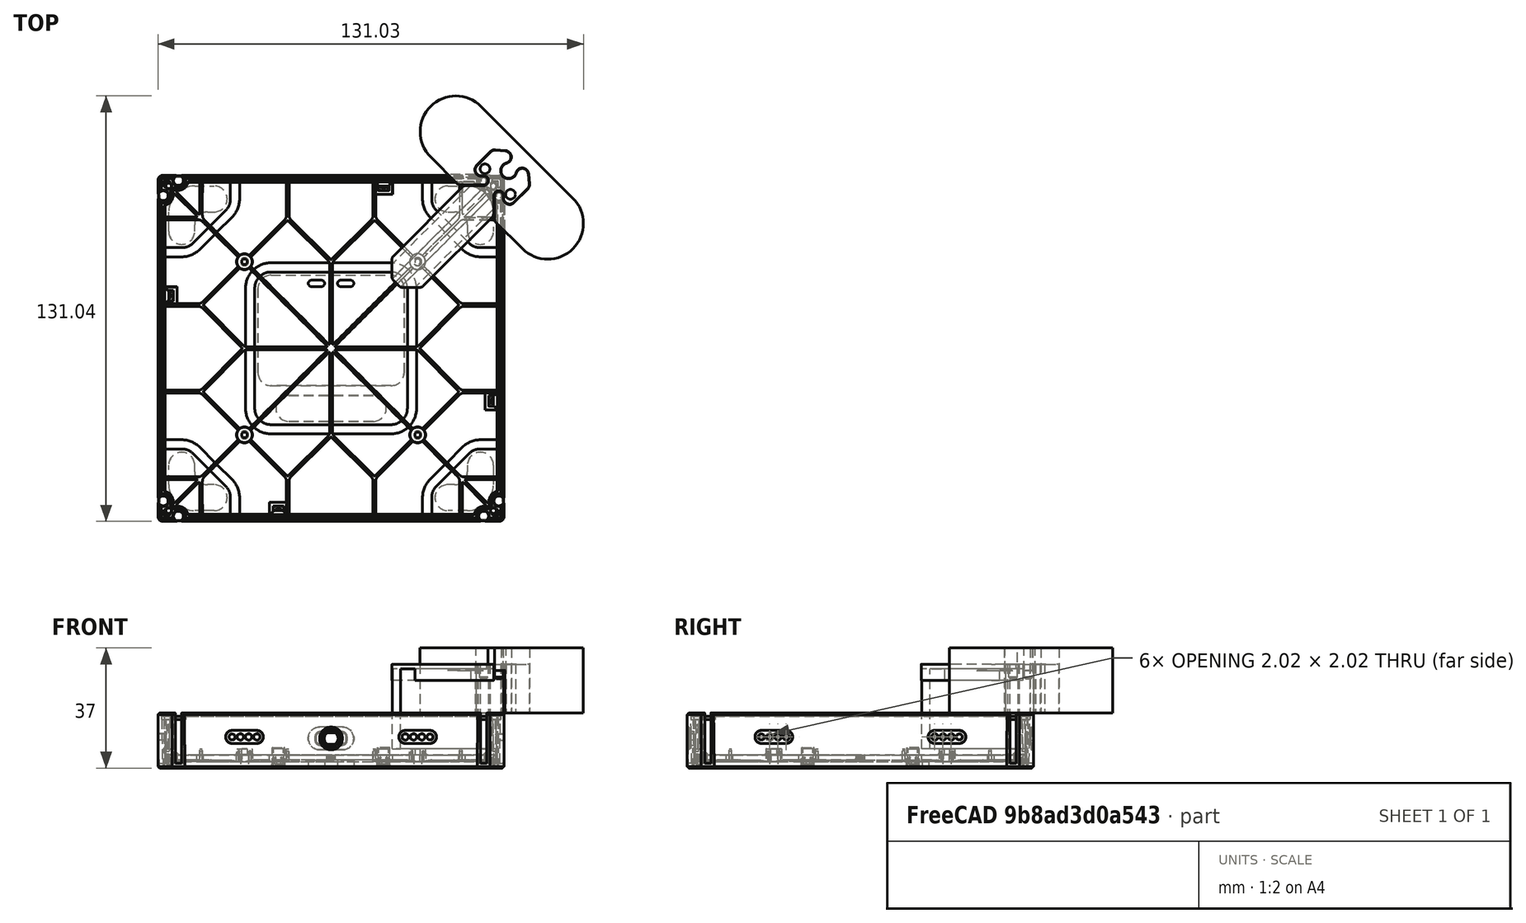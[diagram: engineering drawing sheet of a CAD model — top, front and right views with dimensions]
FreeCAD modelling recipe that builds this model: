
FCSTD DOCUMENT  (FreeCAD 0.21R33771 (Git))
Label: magnet_press_jig_2 part_assy_v3
License: All rights reserved
LicenseURL: https://en.wikipedia.org/wiki/All_rights_reserved
objects: App::FeaturePython×4, Part::FeaturePython×2, Sketcher::SketchObject×1, PartDesign::Body×1
note: 4 computed .brp shape members not serialized (recipe doc carries the construction recipe); baked Part::Feature solids carry a one-line shape summary decoded from their .brp

FEATURE [Part::FeaturePython] b_PLASTIC_CANVAS_001_  label="PLASTIC-CANVAS_001"  # a2plus imported part (geometry in sourceFile) (typed FeaturePython)
  a2p_Version = 0.4.61
  fixedPosition = true
  objectType = a2pPart
  sourceFile = .\..\Mechanical\Design\PLASTIC-CANVAS\PLASTIC-CANVAS.FCStd
  subassemblyImport = false
  timeLastImport = 1.70481e+09
  updateColors = true
FEATURE [Sketcher::SketchObject] Sketch
  FullyConstrained = true
  MapMode = 5
  Support = -> [XY_Plane]
FEATURE [PartDesign::Body] Body
  Group = -> [Sketch]
  Origin = -> Origin
FEATURE [Part::FeaturePython] b_magnet_press_jig_side_2_part_v3_001_  label="magnet_press_jig_side_2 part_v3_001"  # a2plus imported part (geometry in sourceFile) (typed FeaturePython)
  Placement = pos=(51.8768,51.8861,1.5) rot=(0,0,-1;0.785398rad)
  a2p_Version = 0.4.65
  fixedPosition = false
  objectType = a2pPart
  sourceFile = .\magnet_press_jig_side_2 part_v3.FCStd
  subassemblyImport = false
  timeLastImport = 1.72377e+09
  updateColors = true
FEATURE [App::FeaturePython] planeCoincident_001  label="planeCoincident_001__PLASTIC-CANVAS_001"  # a2plus constraint (typed FeaturePython)
  Object1 = b_magnet_press_jig_side_2_part_v3_001_
  Object2 = b_PLASTIC_CANVAS_001_
  ParentTreeObject = -> b_magnet_press_jig_side_2_part_v3_001_
  SubElement1 = Face13
  SubElement2 = Face332
  Suppressed = false
  Type = plane
  directionConstraint = 1
  offset = 0
FEATURE [App::FeaturePython] planeCoincident_001_mirror  label="planeCoincident_001__magnet_press_jig_side_2 part_v3_001"  # a2plus constraint (typed FeaturePython)
  Object1 = b_magnet_press_jig_side_2_part_v3_001_
  Object2 = b_PLASTIC_CANVAS_001_
  ParentTreeObject = -> b_PLASTIC_CANVAS_001_
  SubElement1 = Face13
  SubElement2 = Face332
  Suppressed = false
  Type = plane
  directionConstraint = 1
  offset = 0
FEATURE [App::FeaturePython] axisCoincident_001  label="axisCoincident_001__PLASTIC-CANVAS_001"  # a2plus constraint (typed FeaturePython)
  Object1 = b_magnet_press_jig_side_2_part_v3_001_
  Object2 = b_PLASTIC_CANVAS_001_
  ParentTreeObject = -> b_magnet_press_jig_side_2_part_v3_001_
  SubElement1 = Edge54
  SubElement2 = Edge1374
  Suppressed = false
  Type = axial
  directionConstraint = 0
  lockRotation = false
FEATURE [App::FeaturePython] axisCoincident_001_mirror  label="axisCoincident_001__magnet_press_jig_side_2 part_v3_001"  # a2plus constraint (typed FeaturePython)
  Object1 = b_magnet_press_jig_side_2_part_v3_001_
  Object2 = b_PLASTIC_CANVAS_001_
  ParentTreeObject = -> b_PLASTIC_CANVAS_001_
  SubElement1 = Edge54
  SubElement2 = Edge1374
  Suppressed = false
  Type = axial
  directionConstraint = 0
  lockRotation = false
